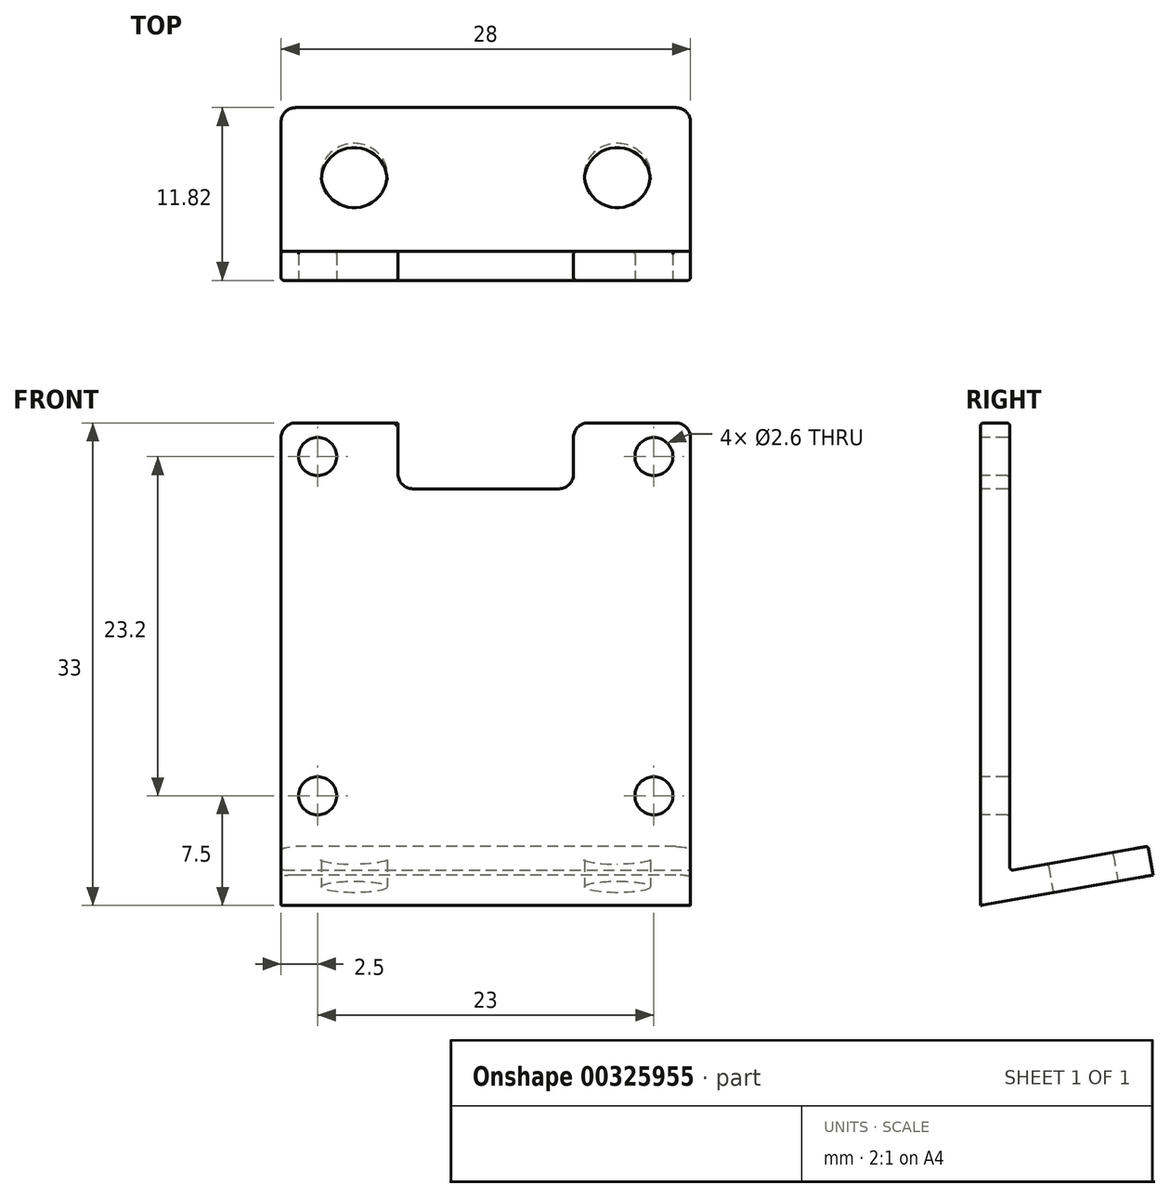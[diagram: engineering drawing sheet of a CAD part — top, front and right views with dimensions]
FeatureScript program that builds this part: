
annotation { "Feature Type Name" : "Feature", "Feature Type Description" : "" }
export const myFeature = defineFeature(function(context is Context, id is Id, definition is map)
    precondition{}
    {
        {
            var Q0;
            Q0=qCreatedBy(makeId("Right.planeOp"),FACE);
            var sketch = newSketch(context, id + "F0", { "sketchPlane" : qUnion([Q0])});
            skLineSegment(sketch, "E0", {"start": v(0, 0) * mm, "end": v(11.82, 2.08) * mm});
            skLineSegment(sketch, "E1.0", {"start": v(2, 2.38) * mm, "end": v(11.47, 4.05) * mm});
            skLineSegment(sketch, "E2", {"start": v(11.47, 4.05) * mm, "end": v(11.82, 2.08) * mm});
            skLineSegment(sketch, "E3.0", {"start": v(2, 33) * mm, "end": v(2, 2.38) * mm});
            skLineSegment(sketch, "E4", {"start": v(0, 33) * mm, "end": v(2, 33) * mm});
            skLineSegment(sketch, "E5", {"start": v(0, 0) * mm, "end": v(0, 33) * mm});
            skLineSegment(sketch, "E6", {"start": v(-8.63, 0) * mm, "end": v(17.14, 0) * mm, "construction": true});
            skSolve(sketch);
        }
        {
            var Q0;
            Q0=makeQuery(id+"F0.imprint","IMPRINT",FACE,{"disambiguationData":[TD([[makeQuery(id+"F0.imprint","IMPRINT",EDGE,{"derivedFrom":sQuery(id+"F0.wireOp",EDGE,"3EGHNGjL-zdSv-KK9s-0Atg-bf2mkZYIS4n5")}),1.0]])]});
            var Q1;
            Q1=makeQuery(id+"F0.imprint","IMPRINT",FACE,{"disambiguationData":[TD([[makeQuery(id+"F0.imprint","IMPRINT",EDGE,{"derivedFrom":sQuery(id+"F0.wireOp",EDGE,"E0")}),1.0]])]});
            extrude(context, id + "F1", {"entities" : qUnion([Q0, Q1]), "endBound" : BoundingType.SYMMETRIC, "depth" : 28 * mm});
        }
        {
            var Q0;
            Q0=qCreatedBy(makeId("Front.planeOp"),FACE);
            var sketch = newSketch(context, id + "F2", { "sketchPlane" : qUnion([Q0])});
            skLineSegment(sketch, "E7", {"start": v(0, 34.62) * mm, "end": v(0, -4.66) * mm, "construction": true});
            skLineSegment(sketch, "E8.0", {"start": v(-11.5, 34.62) * mm, "end": v(-11.5, -4.66) * mm, "construction": true});
            skLineSegment(sketch, "E9.MirrorCS", {"start": v(11.5, 34.62) * mm, "end": v(11.5, -4.66) * mm, "construction": true});
            skLineSegment(sketch, "E10.0", {"start": v(14, 30.7) * mm, "end": v(-14, 30.7) * mm, "construction": true});
            skLineSegment(sketch, "E11.0", {"start": v(14, 7.5) * mm, "end": v(-14, 7.5) * mm, "construction": true});
            skLineSegment(sketch, "E12.0", {"start": v(-6, 34.62) * mm, "end": v(-6, -4.66) * mm, "construction": true});
            skLineSegment(sketch, "E13.MirrorCS", {"start": v(6, 34.62) * mm, "end": v(6, -4.66) * mm, "construction": true});
            skPoint(sketch, "E14", {"position": v(11.5, 30.7) * mm});
            skPoint(sketch, "E15", {"position": v(-11.5, 30.7) * mm});
            skPoint(sketch, "E16", {"position": v(-11.5, 7.5) * mm});
            skPoint(sketch, "E17", {"position": v(11.5, 7.5) * mm});
            skLineSegment(sketch, "E18.0", {"start": v(14, 28.5) * mm, "end": v(-14, 28.5) * mm, "construction": true});
            skLineSegment(sketch, "E19.0", {"start": v(14, 33) * mm, "end": v(-14, 33) * mm, "construction": true});
            skLineSegment(sketch, "E20.bottom", {"start": v(-6, 33) * mm, "end": v(6, 33) * mm});
            skLineSegment(sketch, "E20.top", {"start": v(-6, 28.5) * mm, "end": v(6, 28.5) * mm});
            skLineSegment(sketch, "E20.left", {"start": v(-6, 33) * mm, "end": v(-6, 28.5) * mm});
            skLineSegment(sketch, "E20.right", {"start": v(6, 33) * mm, "end": v(6, 28.5) * mm});
            skSolve(sketch);
        }
        {
            var Q0;
            Q0=makeQuery(id+"F2.imprint","IMPRINT",FACE,{"disambiguationData":[TD([[makeQuery(id+"F2.imprint","IMPRINT",EDGE,{"derivedFrom":sQuery(id+"F2.wireOp",EDGE,"E20.bottom")}),-1.0]])]});
            extrude(context, id + "F3", {"entities" : qUnion([Q0]), "operationType" : NewBodyOperationType.REMOVE, "oppositeDirection" : true, "depth" : 25 * mm});
        }
        {
            var Q0;
            Q0=sQuery(id+"F2.wireOp",VERTEX,"E15");
            var Q1;
            Q1=sQuery(id+"F2.wireOp",VERTEX,"E14");
            var Q2;
            Q2=sQuery(id+"F2.wireOp",VERTEX,"E17");
            var Q3;
            Q3=sQuery(id+"F2.wireOp",VERTEX,"E16");
            var Q4;
            Q4=makeQuery(id+"F1.opExtrude","SWEPT_BODY",BODY,{"disambiguationData":[OSD([sQuery(id+"F0.wireOp",EDGE,"3EGHNGjL-zdSv-KK9s-0Atg-bf2mkZYIS4n5"),sQuery(id+"F0.wireOp",EDGE,"E0"),sQuery(id+"F0.wireOp",EDGE,"E1.0"),sQuery(id+"F0.wireOp",EDGE,"E2"),sQuery(id+"F0.wireOp",EDGE,"E3.0"),sQuery(id+"F0.wireOp",EDGE,"RQ9TA9ig-hEbg-km5D-VRTo-yYHis3AQJvj9"),sQuery(id+"F0.wireOp",EDGE,"E4")])]});
            hole(context, id + "F4", {"style" : HoleStyle.SIMPLE, "endStyle" : HoleEndStyle.THROUGH, "holeDiameter" : 2.6 * mm, "tappedDepth" : 12 * mm, "tapClearance" : 3, "startFromSketch" : true, "locations" : qUnion([Q0, Q1, Q2, Q3]), "scope" : qUnion([Q4])});
        }
        {
            var Q0;
            Q0=makeQuery(id+"F1.opExtrude","SWEPT_FACE",FACE,{"disambiguationData":[OSD([sQuery(id+"F0.wireOp",EDGE,"E0")])]});
            var sketch = newSketch(context, id + "F5", { "sketchPlane" : qUnion([Q0])});
            skLineSegment(sketch, "E21.0", {"start": v(14, -7.3) * mm, "end": v(-14, -7.3) * mm, "construction": true});
            skLineSegment(sketch, "E22.0", {"start": v(-9, 0) * mm, "end": v(-9, -12) * mm, "construction": true});
            skLineSegment(sketch, "E23.0", {"start": v(9, 0) * mm, "end": v(9, -12) * mm, "construction": true});
            skPoint(sketch, "E24", {"position": v(-9, -7.3) * mm});
            skPoint(sketch, "E25", {"position": v(9, -7.3) * mm});
            skSolve(sketch);
        }
        {
            var Q0;
            Q0=sQuery(id+"F5.wireOp",VERTEX,"E24");
            var Q1;
            Q1=sQuery(id+"F5.wireOp",VERTEX,"E25");
            var Q2;
            Q2=makeQuery(id+"F1.opExtrude","SWEPT_BODY",BODY,{"disambiguationData":[OSD([sQuery(id+"F0.wireOp",EDGE,"3EGHNGjL-zdSv-KK9s-0Atg-bf2mkZYIS4n5"),sQuery(id+"F0.wireOp",EDGE,"E0"),sQuery(id+"F0.wireOp",EDGE,"E1.0"),sQuery(id+"F0.wireOp",EDGE,"E2"),sQuery(id+"F0.wireOp",EDGE,"E3.0"),sQuery(id+"F0.wireOp",EDGE,"RQ9TA9ig-hEbg-km5D-VRTo-yYHis3AQJvj9"),sQuery(id+"F0.wireOp",EDGE,"E4")])]});
            hole(context, id + "F6", {"style" : HoleStyle.SIMPLE, "endStyle" : HoleEndStyle.BLIND, "holeDiameter" : 4.5 * mm, "holeDepth" : 3 * mm, "tappedDepth" : 12 * mm, "tapClearance" : 3, "startFromSketch" : true, "locations" : qUnion([Q0, Q1]), "scope" : qUnion([Q2])});
        }
        {
            var Q0;
            Q0=makeQuery(id+"F3.boolean.opBoolean","COPY",EDGE,{"derivedFrom":makeQuery(id+"F3.opExtrude","SWEPT_EDGE",EDGE,{"disambiguationData":[OSD([sQuery(id+"F2.wireOp",EDGE,"NbHmLuiW-MSQV-WUPs-HCHp-j8KwECjTilKN.top"),sQuery(id+"F2.wireOp",EDGE,"NbHmLuiW-MSQV-WUPs-HCHp-j8KwECjTilKN.left")])]})});
            var Q1;
            Q1=makeQuery(id+"F3.boolean.opBoolean","COPY",EDGE,{"derivedFrom":makeQuery(id+"F3.opExtrude","SWEPT_EDGE",EDGE,{"disambiguationData":[OSD([sQuery(id+"F2.wireOp",EDGE,"NbHmLuiW-MSQV-WUPs-HCHp-j8KwECjTilKN.top"),sQuery(id+"F2.wireOp",EDGE,"NbHmLuiW-MSQV-WUPs-HCHp-j8KwECjTilKN.right")])]})});
            var Q2;
            Q2=makeQuery(id+"F3.boolean.opBoolean","COPY",EDGE,{"derivedFrom":makeQuery(id+"F3.opExtrude","SWEPT_EDGE",EDGE,{"disambiguationData":[OSD([sQuery(id+"F2.wireOp",EDGE,"NbHmLuiW-MSQV-WUPs-HCHp-j8KwECjTilKN.bottom"),sQuery(id+"F2.wireOp",EDGE,"NbHmLuiW-MSQV-WUPs-HCHp-j8KwECjTilKN.right")])]})});
            var Q3;
            Q3=makeQuery(id+"F3.boolean.opBoolean","COPY",EDGE,{"derivedFrom":makeQuery(id+"F3.opExtrude","SWEPT_EDGE",EDGE,{"disambiguationData":[OSD([sQuery(id+"F2.wireOp",EDGE,"NbHmLuiW-MSQV-WUPs-HCHp-j8KwECjTilKN.bottom"),sQuery(id+"F2.wireOp",EDGE,"NbHmLuiW-MSQV-WUPs-HCHp-j8KwECjTilKN.left")])]})});
            var Q4;
            Q4=makeQuery(id+"F1.opExtrude","CAP_EDGE",EDGE,{"disambiguationData":[OSD([sQuery(id+"F0.wireOp",EDGE,"E4")])],"isStart":true});
            var Q5;
            Q5=makeQuery(id+"F1.opExtrude","CAP_EDGE",EDGE,{"disambiguationData":[OSD([sQuery(id+"F0.wireOp",EDGE,"E4")])],"isStart":false});
            var Q6;
            Q6=makeQuery(id+"F1.opExtrude","CAP_EDGE",EDGE,{"disambiguationData":[OSD([sQuery(id+"F0.wireOp",EDGE,"E2")])],"isStart":false});
            var Q7;
            Q7=makeQuery(id+"F1.opExtrude","CAP_EDGE",EDGE,{"disambiguationData":[OSD([sQuery(id+"F0.wireOp",EDGE,"E2")])],"isStart":true});
            var Q8;
            Q8=makeQuery(id+"F3.boolean.opBoolean","COPY",EDGE,{"derivedFrom":makeQuery(id+"F3.opExtrude","SWEPT_EDGE",EDGE,{"disambiguationData":[OSD([sQuery(id+"F2.wireOp",EDGE,"E20.bottom"),sQuery(id+"F2.wireOp",EDGE,"E20.right")])]})});
            var Q9;
            Q9=makeQuery(id+"F3.boolean.opBoolean","COPY",EDGE,{"derivedFrom":makeQuery(id+"F3.opExtrude","SWEPT_EDGE",EDGE,{"disambiguationData":[OSD([sQuery(id+"F2.wireOp",EDGE,"E20.bottom"),sQuery(id+"F2.wireOp",EDGE,"E20.left")])]})});
            var Q10;
            Q10=makeQuery(id+"F3.boolean.opBoolean","COPY",EDGE,{"derivedFrom":makeQuery(id+"F3.opExtrude","SWEPT_EDGE",EDGE,{"disambiguationData":[OSD([sQuery(id+"F2.wireOp",EDGE,"E20.top"),sQuery(id+"F2.wireOp",EDGE,"E20.right")])]})});
            var Q11;
            Q11=makeQuery(id+"F3.boolean.opBoolean","COPY",EDGE,{"derivedFrom":makeQuery(id+"F3.opExtrude","SWEPT_EDGE",EDGE,{"disambiguationData":[OSD([sQuery(id+"F2.wireOp",EDGE,"E20.top"),sQuery(id+"F2.wireOp",EDGE,"E20.left")])]})});
            fillet(context, id + "F7", {"entities" : qUnion([Q0, Q1, Q2, Q3, Q4, Q5, Q6, Q7, Q8, Q9, Q10, Q11]), "radius" : 1 * mm, "tangentPropagation" : true, "allowEdgeOverflow" : false});
        }
        {
            var Q0;
            Q0=makeQuery(id+"F1.opExtrude","SWEPT_FACE",FACE,{"disambiguationData":[OSD([sQuery(id+"F0.wireOp",EDGE,"E3.0")])]});
            var Q1;
            Q1=makeQuery(id+"F1.opExtrude","SWEPT_FACE",FACE,{"disambiguationData":[OSD([sQuery(id+"F0.wireOp",EDGE,"E1.0")])]});
            var Q2;
            Q2=makeQuery(id+"F6.hole-0.boolean.opBoolean","COPY",EDGE,{"derivedFrom":makeQuery(id+"F6.hole-0.opRevolve","SWEPT_EDGE",EDGE,{"disambiguationData":[OSD([sQuery(id+"F6.hole-0.sketch.wireOp",EDGE,"core_line_2"),sQuery(id+"F6.hole-0.sketch.wireOp",EDGE,"core_line_3")])]})});
            var Q3;
            Q3=makeQuery(id+"F6.hole-1.boolean.opBoolean","COPY",EDGE,{"derivedFrom":makeQuery(id+"F6.hole-1.opRevolve","SWEPT_EDGE",EDGE,{"disambiguationData":[OSD([sQuery(id+"F6.hole-1.sketch.wireOp",EDGE,"core_line_2"),sQuery(id+"F6.hole-1.sketch.wireOp",EDGE,"core_line_3")])]})});
            var Q4;
            Q4=makeQuery(id+"F4.hole-3.boolean.opBoolean","COPY",EDGE,{"derivedFrom":makeQuery(id+"F4.hole-3.opRevolve","SWEPT_EDGE",EDGE,{"disambiguationData":[OSD([sQuery(id+"F4.hole-3.sketch.wireOp",EDGE,"core_line_2"),sQuery(id+"F4.hole-3.sketch.wireOp",EDGE,"core_line_3")])]})});
            var Q5;
            Q5=makeQuery(id+"F4.hole-2.boolean.opBoolean","COPY",EDGE,{"derivedFrom":makeQuery(id+"F4.hole-2.opRevolve","SWEPT_EDGE",EDGE,{"disambiguationData":[OSD([sQuery(id+"F4.hole-2.sketch.wireOp",EDGE,"core_line_2"),sQuery(id+"F4.hole-2.sketch.wireOp",EDGE,"core_line_3")])]})});
            var Q6;
            Q6=makeQuery(id+"F4.hole-0.boolean.opBoolean","COPY",EDGE,{"derivedFrom":makeQuery(id+"F4.hole-0.opRevolve","SWEPT_EDGE",EDGE,{"disambiguationData":[OSD([sQuery(id+"F4.hole-0.sketch.wireOp",EDGE,"core_line_2"),sQuery(id+"F4.hole-0.sketch.wireOp",EDGE,"core_line_3")])]})});
            var Q7;
            Q7=makeQuery(id+"F4.hole-1.boolean.opBoolean","COPY",EDGE,{"derivedFrom":makeQuery(id+"F4.hole-1.opRevolve","SWEPT_EDGE",EDGE,{"disambiguationData":[OSD([sQuery(id+"F4.hole-1.sketch.wireOp",EDGE,"core_line_2"),sQuery(id+"F4.hole-1.sketch.wireOp",EDGE,"core_line_3")])]})});
            var Q8;
            {var subQ0=sQuery(id+"F0.wireOp",EDGE,"E5");var subQ1=sQuery(id+"F0.wireOp",EDGE,"E4");Q8=makeQuery(id+"F3.boolean.opBoolean","SPLIT",EDGE,{"disambiguationData":[TD([makeQuery(id+"F3.opExtrude","SWEPT_FACE",FACE,{"disambiguationData":[OSD([sQuery(id+"F2.wireOp",EDGE,"E20.left")])]})])],"derivedFrom":makeQuery(id+"F1.opExtrude","SWEPT_EDGE",EDGE,{"disambiguationData":[OSD([subQ1,subQ0])]})});}
            var Q9;
            Q9=makeQuery(id+"F3.boolean.opBoolean","COPY",EDGE,{"derivedFrom":makeQuery(id+"F3.opExtrude","CAP_EDGE",EDGE,{"disambiguationData":[OSD([sQuery(id+"F2.wireOp",EDGE,"E20.left")])],"isStart":true})});
            var Q10;
            Q10=makeQuery(id+"F3.boolean.opBoolean","COPY",EDGE,{"derivedFrom":makeQuery(id+"F3.opExtrude","CAP_EDGE",EDGE,{"disambiguationData":[OSD([sQuery(id+"F2.wireOp",EDGE,"E20.top")])],"isStart":true})});
            var Q11;
            Q11=makeQuery(id+"F3.boolean.opBoolean","COPY",EDGE,{"derivedFrom":makeQuery(id+"F3.opExtrude","CAP_EDGE",EDGE,{"disambiguationData":[OSD([sQuery(id+"F2.wireOp",EDGE,"E20.right")])],"isStart":true})});
            var Q12;
            {var subQ0=sQuery(id+"F0.wireOp",EDGE,"E5");var subQ1=sQuery(id+"F0.wireOp",EDGE,"E4");Q12=makeQuery(id+"F3.boolean.opBoolean","SPLIT",EDGE,{"disambiguationData":[TD([makeQuery(id+"F3.opExtrude","SWEPT_FACE",FACE,{"disambiguationData":[OSD([sQuery(id+"F2.wireOp",EDGE,"E20.right")])]})])],"derivedFrom":makeQuery(id+"F1.opExtrude","SWEPT_EDGE",EDGE,{"disambiguationData":[OSD([subQ1,subQ0])]})});}
            var Q13;
            Q13=makeQuery(id+"F1.opExtrude","CAP_EDGE",EDGE,{"disambiguationData":[OSD([sQuery(id+"F0.wireOp",EDGE,"E5")])],"isStart":false});
            var Q14;
            Q14=makeQuery(id+"F1.opExtrude","CAP_EDGE",EDGE,{"disambiguationData":[OSD([sQuery(id+"F0.wireOp",EDGE,"E5")])],"isStart":true});
            fillet(context, id + "F8", {"entities" : qUnion([Q0, Q1, Q2, Q3, Q4, Q5, Q6, Q7, Q8, Q9, Q10, Q11, Q12, Q13, Q14]), "radius" : 0.2 * mm, "tangentPropagation" : true, "allowEdgeOverflow" : false});
        }
    });
